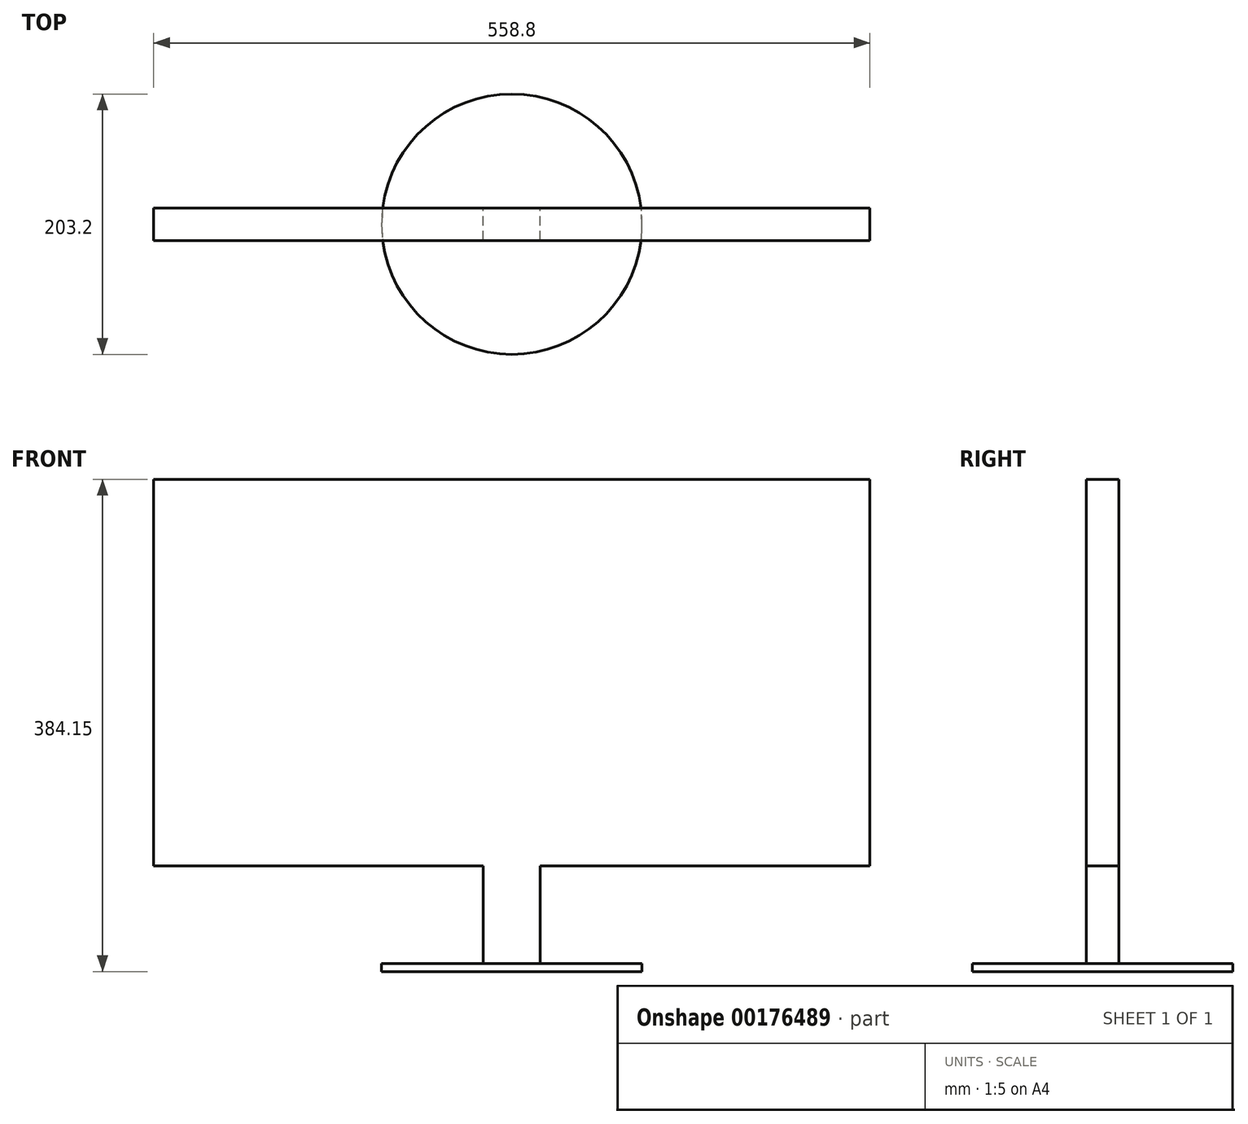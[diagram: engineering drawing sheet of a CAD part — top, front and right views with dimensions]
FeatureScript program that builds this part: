
annotation { "Feature Type Name" : "Feature", "Feature Type Description" : "" }
export const myFeature = defineFeature(function(context is Context, id is Id, definition is map)
    precondition{}
    {
        {
            var Q0;
            Q0=qCreatedBy(makeId("Front.planeOp"),FACE);
            var sketch = newSketch(context, id + "F0", { "sketchPlane" : qUnion([Q0])});
            skLineSegment(sketch, "E0.bottom", {"start": v(279.4, 150.8) * mm, "end": v(-279.4, 150.8) * mm});
            skLineSegment(sketch, "E0.top", {"start": v(279.4, -150.8) * mm, "end": v(-279.4, -150.8) * mm});
            skLineSegment(sketch, "E0.left", {"start": v(279.4, 150.8) * mm, "end": v(279.4, -150.8) * mm});
            skLineSegment(sketch, "E0.right", {"start": v(-279.4, 150.8) * mm, "end": v(-279.4, -150.8) * mm});
            skPoint(sketch, "E0.middle", {"position": v(0, 0) * mm});
            skLineSegment(sketch, "E1", {"start": v(-279.4, 150.8) * mm, "end": v(279.4, -150.8) * mm});
            skLineSegment(sketch, "E2.top", {"start": v(22.23, -227) * mm, "end": v(-22.22, -227) * mm});
            skLineSegment(sketch, "E2.left", {"start": v(22.23, -150.8) * mm, "end": v(22.23, -227) * mm});
            skLineSegment(sketch, "E2.right", {"start": v(-22.22, -150.8) * mm, "end": v(-22.22, -227) * mm});
            skPoint(sketch, "E2.middle", {"position": v(0, -150.8) * mm});
            skSolve(sketch);
        }
        {
            var Q0;
            Q0 = qSketchRegion(id + "F0", true);
            extrude(context, id + "F1", {"entities" : qUnion([Q0]), "endBound" : BoundingType.SYMMETRIC, "depth" : 25.4 * mm});
        }
        {
            var Q0;
            Q0=makeQuery(id+"F1.opExtrude","SWEPT_FACE",FACE,{"disambiguationData":[OSD([sQuery(id+"F0.wireOp",EDGE,"E2.top")])]});
            var sketch = newSketch(context, id + "F2", { "sketchPlane" : qUnion([Q0])});
            skCircle(sketch, "E3", {"center": v(0, 0) * mm, "radius": 101.6 * mm});
            skSolve(sketch);
        }
        {
            var Q0;
            Q0 = qSketchRegion(id + "F2", true);
            extrude(context, id + "F3", {"entities" : qUnion([Q0]), "operationType" : NewBodyOperationType.ADD, "depth" : 6.35 * mm});
        }
    });
